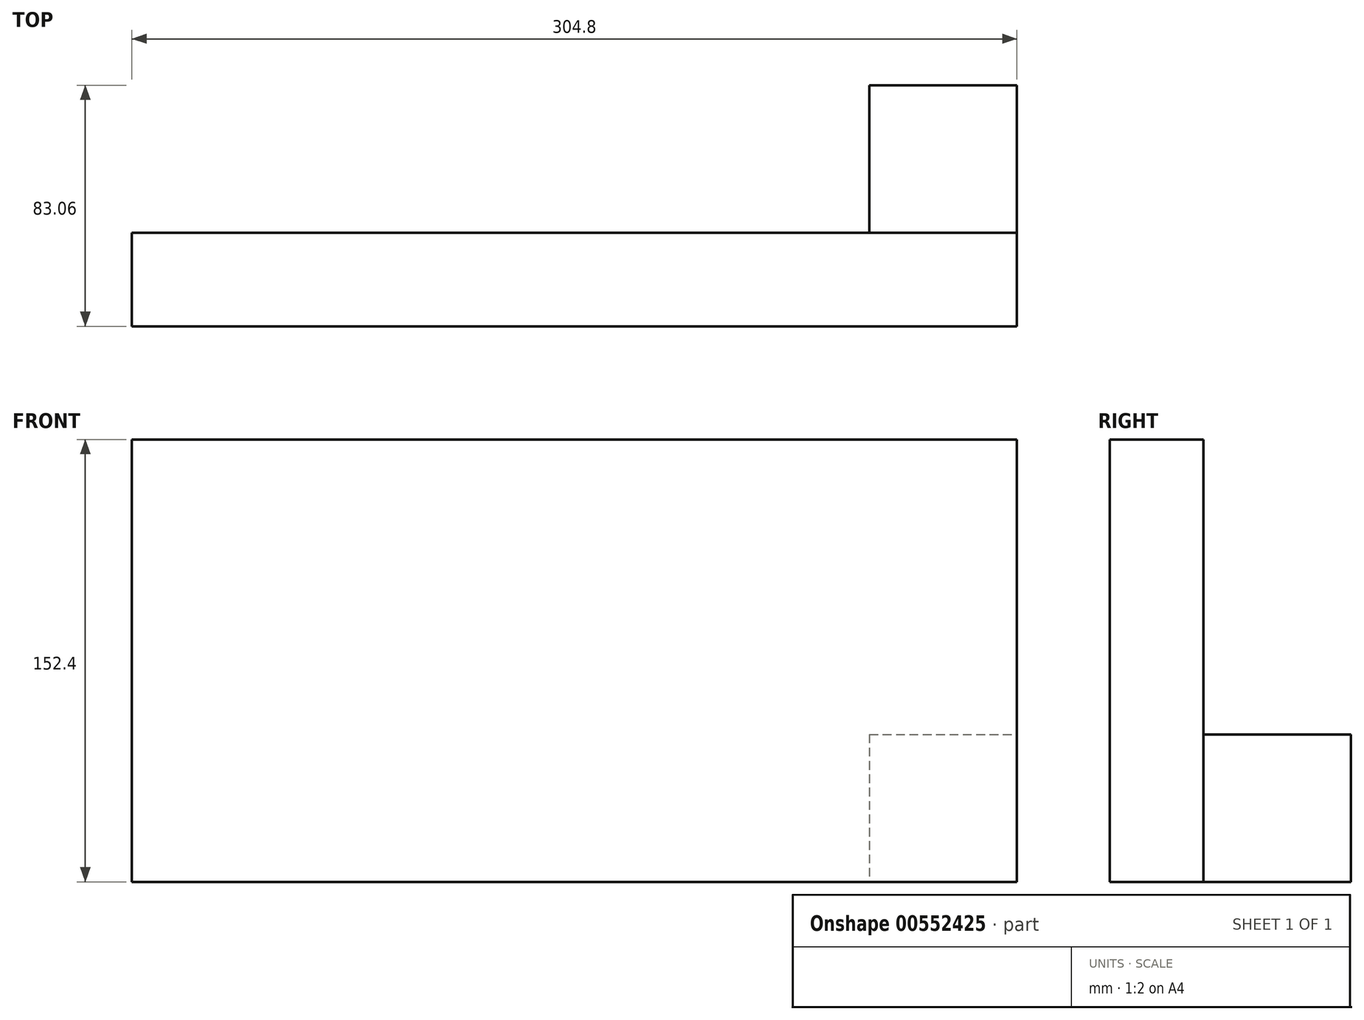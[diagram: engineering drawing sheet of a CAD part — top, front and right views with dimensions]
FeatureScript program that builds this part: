
annotation { "Feature Type Name" : "Feature", "Feature Type Description" : "" }
export const myFeature = defineFeature(function(context is Context, id is Id, definition is map)
    precondition{}
    {
        {
            var Q0;
            Q0=qCreatedBy(makeId("Front.planeOp"),FACE);
            var sketch = newSketch(context, id + "F0", { "sketchPlane" : qUnion([Q0])});
            skLineSegment(sketch, "E0.bottom", {"start": v(-202.46, 69.27) * mm, "end": v(102.34, 69.27) * mm});
            skLineSegment(sketch, "E0.top", {"start": v(-202.46, -83.13) * mm, "end": v(102.34, -83.13) * mm});
            skLineSegment(sketch, "E0.left", {"start": v(-202.46, 69.27) * mm, "end": v(-202.46, -83.13) * mm});
            skLineSegment(sketch, "E0.right", {"start": v(102.34, 69.27) * mm, "end": v(102.34, -83.13) * mm});
            skSolve(sketch);
        }
        {
            var Q0;
            Q0=makeQuery(id+"F0.imprint","IMPRINT",FACE,{"disambiguationData":[TD([[makeQuery(id+"F0.imprint","IMPRINT",EDGE,{"derivedFrom":sQuery(id+"F0.wireOp",EDGE,"E0.bottom")}),-1.0]])]});
            extrude(context, id + "F1", {"entities" : qUnion([Q0]), "oppositeDirection" : true, "depth" : 32.26 * mm, "offsetDistance" : 25.4 * mm});
        }
        {
            var Q0;
            Q0=makeQuery(id+"F1.opExtrude","CAP_FACE",FACE,{"disambiguationData":[OSD([sQuery(id+"F0.wireOp",EDGE,"E0.bottom"),sQuery(id+"F0.wireOp",EDGE,"E0.top"),sQuery(id+"F0.wireOp",EDGE,"E0.left"),sQuery(id+"F0.wireOp",EDGE,"E0.right")])],"isStart":false});
            var sketch = newSketch(context, id + "F2", { "sketchPlane" : qUnion([Q0])});
            skLineSegment(sketch, "E1.bottom", {"start": v(-51.53, -32.32) * mm, "end": v(-102.33, -32.32) * mm});
            skLineSegment(sketch, "E1.top", {"start": v(-51.53, -83.12) * mm, "end": v(-102.33, -83.12) * mm});
            skLineSegment(sketch, "E1.left", {"start": v(-51.53, -32.32) * mm, "end": v(-51.53, -83.12) * mm});
            skLineSegment(sketch, "E1.right", {"start": v(-102.33, -32.32) * mm, "end": v(-102.33, -83.12) * mm});
            skSolve(sketch);
        }
        {
            var Q0;
            {var subQ0=sQuery(id+"F2.wireOp",EDGE,"E1.top");Q0=makeQuery(id+"F2.imprint","IMPRINT",FACE,{"disambiguationData":[TD([[makeQuery(id+"F2.imprint","IMPRINT",EDGE,{"derivedFrom":subQ0}),-1.0]])]});}
            var Q1;
            {var subQ0=sQuery(id+"F2.wireOp",EDGE,"E1.bottom");Q1=makeQuery(id+"F2.imprint","IMPRINT",FACE,{"disambiguationData":[TD([[makeQuery(id+"F2.imprint","IMPRINT",EDGE,{"derivedFrom":subQ0}),1.0]])]});}
            extrude(context, id + "F3", {"entities" : qUnion([Q0, Q1]), "operationType" : NewBodyOperationType.ADD, "depth" : 50.8 * mm, "offsetDistance" : 25.4 * mm});
        }
    });
